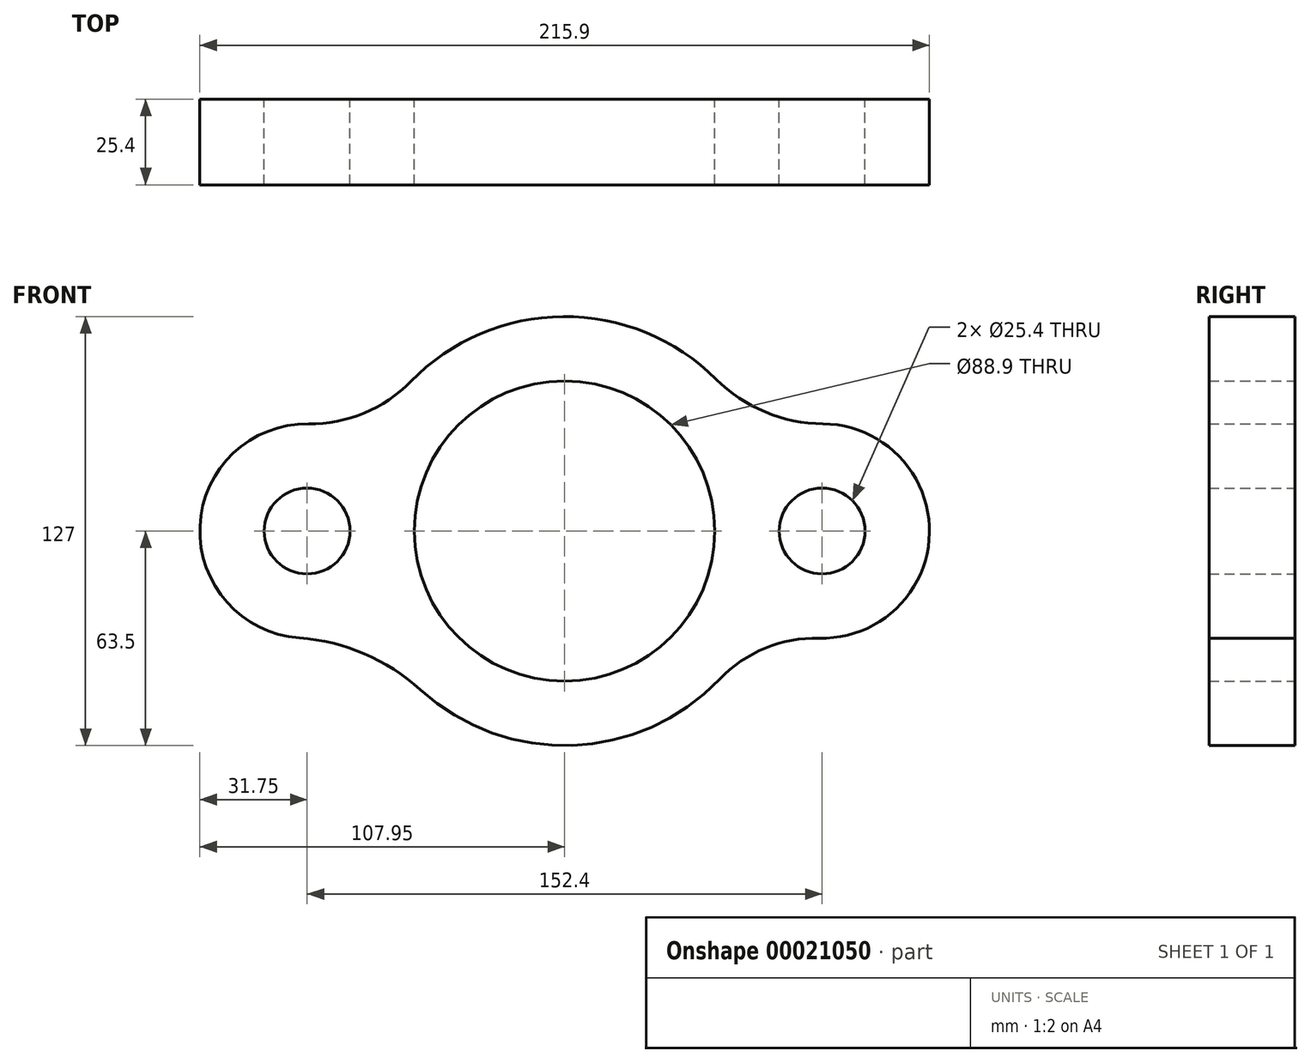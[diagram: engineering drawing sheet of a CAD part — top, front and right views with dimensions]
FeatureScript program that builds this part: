
annotation { "Feature Type Name" : "Feature", "Feature Type Description" : "" }
export const myFeature = defineFeature(function(context is Context, id is Id, definition is map)
    precondition{}
    {
        {
            var Q0;
            Q0=qCreatedBy(makeId("Front.planeOp"),FACE);
            var sketch = newSketch(context, id + "F0", { "sketchPlane" : qUnion([Q0])});
            skArc(sketch, "E0", {"start": v(-42.7, -47) * mm, "mid": v(2.24, -63.46) * mm, "end": v(45.91, -43.87) * mm});
            skCircle(sketch, "E1", {"center": v(0, 0) * mm, "radius": 44.45 * mm});
            skCircle(sketch, "E2", {"center": v(76.2, 0) * mm, "radius": 12.7 * mm});
            skCircle(sketch, "E3", {"center": v(-76.2, 0) * mm, "radius": 12.7 * mm});
            skArc(sketch, "E4", {"start": v(-75.78, 31.75) * mm, "mid": v(-107.92, 1.35) * mm, "end": v(-78.48, -31.67) * mm});
            skArc(sketch, "E5", {"start": v(75.35, -31.74) * mm, "mid": v(107.95, -0.55) * mm, "end": v(76.45, 31.75) * mm});
            skArc(sketch, "E6", {"start": v(-75.78, 31.75) * mm, "mid": v(-59.35, 34.9) * mm, "end": v(-45.5, 44.3) * mm});
            skArc(sketch, "E7", {"start": v(44.84, 44.96) * mm, "mid": v(59.35, 35.25) * mm, "end": v(76.45, 31.75) * mm});
            skArc(sketch, "E8", {"start": v(75.35, -31.74) * mm, "mid": v(59.35, -34.68) * mm, "end": v(45.91, -43.87) * mm});
            skArc(sketch, "E9", {"start": v(-42.7, -47) * mm, "mid": v(-59.3, -36.33) * mm, "end": v(-78.48, -31.67) * mm});
            skArc(sketch, "E10.trimOffspring", {"start": v(44.84, 44.96) * mm, "mid": v(-0.47, 63.5) * mm, "end": v(-45.5, 44.3) * mm});
            skSolve(sketch);
        }
        {
            var Q0;
            Q0 = qSketchRegion(id + "F0", true);
            extrude(context, id + "F1", {"entities" : qUnion([Q0]), "depth" : 25.4 * mm});
        }
        {
            var Q0;
            Q0=makeQuery(id+"F0.imprint","IMPRINT",FACE,{"disambiguationData":[TD([[makeQuery(id+"F0.imprint","IMPRINT",EDGE,{"derivedFrom":sQuery(id+"F0.wireOp",EDGE,"E0")}),1.0]])]});
            extrude(context, id + "F2", {"entities" : qUnion([Q0]), "operationType" : NewBodyOperationType.ADD, "depth" : 25.4 * mm});
        }
    });
